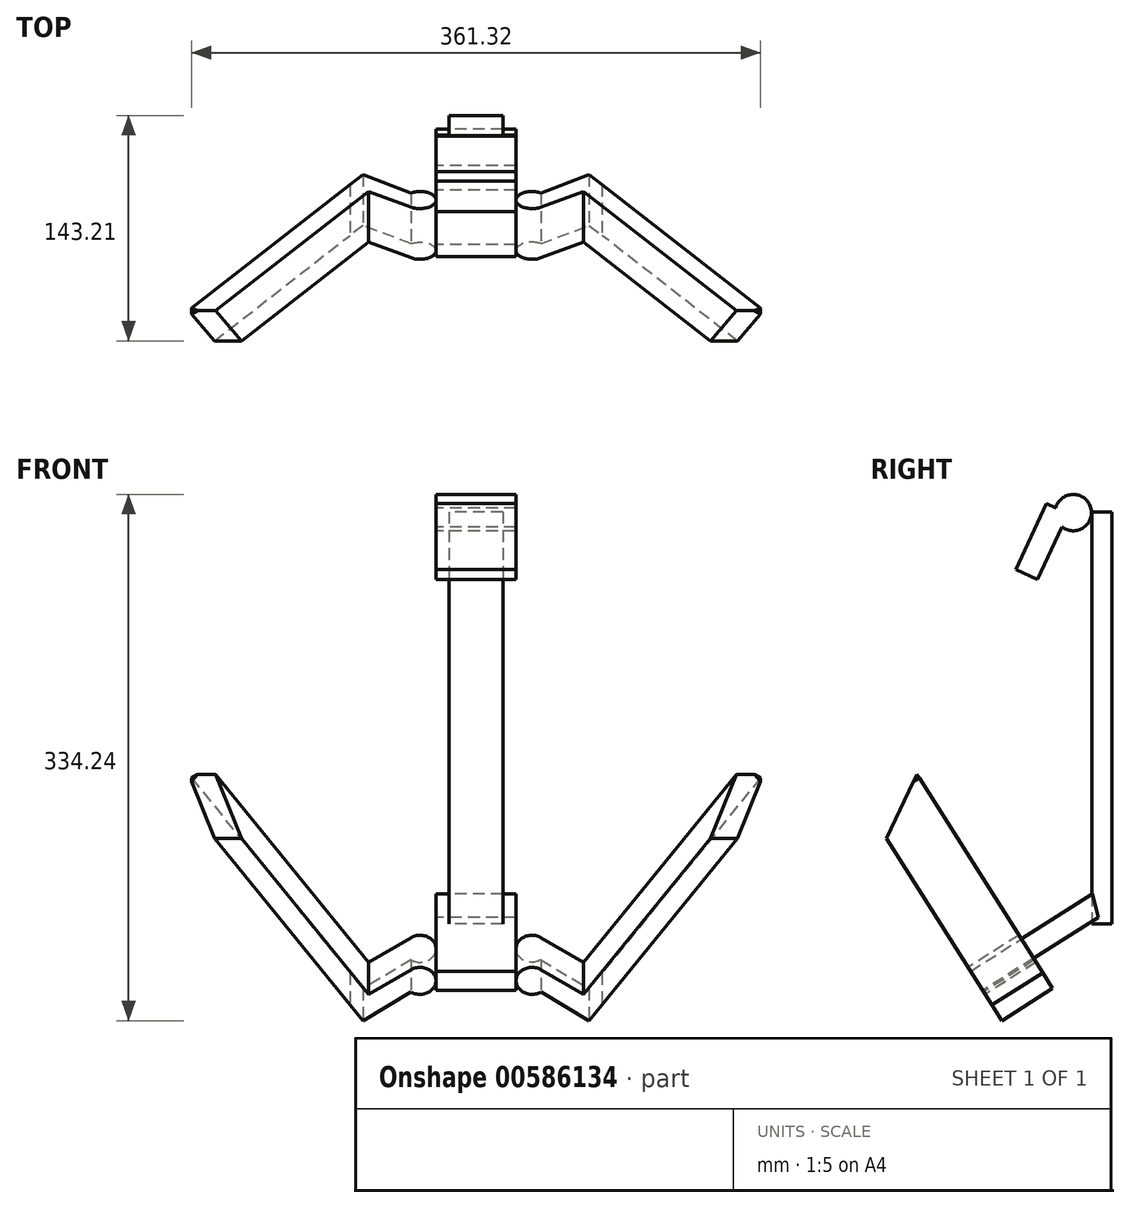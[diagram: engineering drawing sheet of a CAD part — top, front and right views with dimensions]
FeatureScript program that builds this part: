
annotation { "Feature Type Name" : "Feature", "Feature Type Description" : "" }
export const myFeature = defineFeature(function(context is Context, id is Id, definition is map)
    precondition{}
    {
        {
            var Q0;
            Q0=qCreatedBy(makeId("Front.planeOp"),FACE);
            var sketch = newSketch(context, id + "F0", { "sketchPlane" : qUnion([Q0])});
            skLineSegment(sketch, "E0.bottom", {"start": v(17.06, 130.82) * mm, "end": v(-17.06, 130.82) * mm});
            skLineSegment(sketch, "E0.top", {"start": v(17.06, -130.82) * mm, "end": v(-17.06, -130.82) * mm});
            skLineSegment(sketch, "E0.left", {"start": v(17.06, 130.82) * mm, "end": v(17.06, -130.82) * mm});
            skLineSegment(sketch, "E0.right", {"start": v(-17.06, 130.82) * mm, "end": v(-17.06, -130.82) * mm});
            skPoint(sketch, "E0.middle", {"position": v(0, 0) * mm});
            skSolve(sketch);
        }
        {
            var Q0;
            Q0 = qSketchRegion(id + "F0", true);
            extrude(context, id + "F1", {"entities" : qUnion([Q0]), "depth" : 12.7 * mm, "offsetDistance" : 25.4 * mm});
        }
        {
            var Q0;
            Q0=qCreatedBy(makeId("Right.planeOp"),FACE);
            var sketch = newSketch(context, id + "F2", { "sketchPlane" : qUnion([Q0])});
            skCircle(sketch, "E1", {"center": v(-24.55, 130.32) * mm, "radius": 11.55 * mm});
            skLineSegment(sketch, "E2", {"start": v(-31.77, 121.3) * mm, "end": v(-47.3, 87.72) * mm});
            skLineSegment(sketch, "E3", {"start": v(-47.3, 87.72) * mm, "end": v(-61.05, 94.08) * mm});
            skLineSegment(sketch, "E4", {"start": v(-61.05, 94.08) * mm, "end": v(-41.65, 136.02) * mm});
            skLineSegment(sketch, "E5", {"start": v(-41.65, 136.02) * mm, "end": v(-35.72, 133.28) * mm});
            skSolve(sketch);
        }
        {
            var Q0;
            Q0 = qSketchRegion(id + "F2", true);
            extrude(context, id + "F3", {"entities" : qUnion([Q0]), "depth" : 25.4 * mm, "offsetDistance" : 25.4 * mm, "hasSecondDirection" : true, "secondDirectionOppositeDirection" : true, "secondDirectionDepth" : 25.4 * mm});
        }
        {
            var Q0;
            Q0=makeQuery(id+"F3.opExtrude","SWEPT_BODY",BODY,{"disambiguationData":[OSD([sQuery(id+"F2.wireOp",EDGE,"E1"),sQuery(id+"F2.wireOp",EDGE,"E2"),sQuery(id+"F2.wireOp",EDGE,"E3"),sQuery(id+"F2.wireOp",EDGE,"E4"),sQuery(id+"F2.wireOp",EDGE,"E5")])]});
            var Q1;
            Q1=qCreatedBy(makeId("Top.planeOp"),FACE);
            mirror(context, id + "F4", {"entities" : qUnion([Q0]), "mirrorPlane" : qUnion([Q1])});
        }
        {
            var Q0;
            Q0=makeQuery(id+"F4.opPattern","COPY",BODY,{"derivedFrom":makeQuery(id+"F3.opExtrude","SWEPT_BODY",BODY,{"disambiguationData":[OSD([sQuery(id+"F2.wireOp",EDGE,"E1"),sQuery(id+"F2.wireOp",EDGE,"E2"),sQuery(id+"F2.wireOp",EDGE,"E3"),sQuery(id+"F2.wireOp",EDGE,"E4"),sQuery(id+"F2.wireOp",EDGE,"E5")])]}),"instanceName":"1"});
            deleteBodies(context, id + "F5", {"entities" : qUnion([Q0])});
        }
        {
            var Q0;
            Q0=qCreatedBy(makeId("Right.planeOp"),FACE);
            var sketch = newSketch(context, id + "F6", { "sketchPlane" : qUnion([Q0])});
            skLineSegment(sketch, "E6", {"start": v(-37.8, -145.19) * mm, "end": v(-82.02, -173.2) * mm});
            skLineSegment(sketch, "E7", {"start": v(-82.02, -173.2) * mm, "end": v(-89.77, -160.96) * mm});
            skLineSegment(sketch, "E8", {"start": v(-89.77, -160.96) * mm, "end": v(-46.36, -133.47) * mm});
            skLineSegment(sketch, "E9", {"start": v(-46.36, -133.47) * mm, "end": v(-12.31, -111.9) * mm});
            skLineSegment(sketch, "E10", {"start": v(-37.8, -145.19) * mm, "end": v(-8.51, -126.64) * mm});
            skLineSegment(sketch, "E11", {"start": v(-8.51, -126.64) * mm, "end": v(-12.31, -111.9) * mm});
            skSolve(sketch);
        }
        {
            var Q0;
            Q0 = qSketchRegion(id + "F6", true);
            extrude(context, id + "F7", {"entities" : qUnion([Q0]), "depth" : 25.4 * mm, "offsetDistance" : 25.4 * mm, "hasSecondDirection" : true, "secondDirectionOppositeDirection" : true, "secondDirectionDepth" : 25.4 * mm});
        }
        {
            var Q0;
            Q0=makeQuery(id+"F7.opExtrude","SWEPT_FACE",FACE,{"disambiguationData":[OSD([sQuery(id+"F6.wireOp",EDGE,"E7")])]});
            var sketch = newSketch(context, id + "F8", { "sketchPlane" : qUnion([Q0])});
            skCircle(sketch, "E12", {"center": v(-35.54, -95.2) * mm, "radius": 10.14 * mm});
            skPoint(sketch, "E12.centerSnap0", {"position": v(-25.4, -95.2) * mm});
            skLineSegment(sketch, "E13", {"start": v(-41.21, -103.6) * mm, "end": v(-71.78, -125.13) * mm});
            skLineSegment(sketch, "E14", {"start": v(-71.78, -125.13) * mm, "end": v(-80.02, -113.44) * mm});
            skLineSegment(sketch, "E15", {"start": v(-80.02, -113.44) * mm, "end": v(-41.28, -86.84) * mm});
            skSolve(sketch);
        }
        {
            var Q0;
            Q0 = qSketchRegion(id + "F8", true);
            extrude(context, id + "F9", {"entities" : qUnion([Q0]), "operationType" : NewBodyOperationType.ADD, "oppositeDirection" : true, "depth" : 38.1 * mm, "offsetDistance" : 25.4 * mm});
        }
        {
            var Q0;
            Q0=makeQuery(id+"F9.opExtrude","SWEPT_BODY",BODY,{"disambiguationData":[OSD([sQuery(id+"F8.wireOp",EDGE,"E12"),sQuery(id+"F8.wireOp",EDGE,"E13"),sQuery(id+"F8.wireOp",EDGE,"E14"),sQuery(id+"F8.wireOp",EDGE,"E15")])]});
            var Q1;
            Q1=qCreatedBy(makeId("Right.planeOp"),FACE);
            mirror(context, id + "F10", {"operationType" : NewBodyOperationType.ADD, "entities" : qUnion([Q0]), "mirrorPlane" : qUnion([Q1])});
        }
        {
            var Q0;
            Q0=makeQuery(id+"F9.opExtrude","SWEPT_FACE",FACE,{"disambiguationData":[OSD([sQuery(id+"F8.wireOp",EDGE,"E15")])]});
            var sketch = newSketch(context, id + "F11", { "sketchPlane" : qUnion([Q0])});
            skLineSegment(sketch, "E16.bottom", {"start": v(-130.17, -123.86) * mm, "end": v(-116.05, -123.86) * mm});
            skLineSegment(sketch, "E16.top", {"start": v(-130.17, -161.96) * mm, "end": v(-116.05, -161.96) * mm});
            skLineSegment(sketch, "E16.left", {"start": v(-130.17, -123.86) * mm, "end": v(-130.17, -161.96) * mm});
            skLineSegment(sketch, "E16.right", {"start": v(-116.05, -123.86) * mm, "end": v(-116.05, -161.96) * mm});
            skSolve(sketch);
        }
        {
            var Q0;
            Q0=makeQuery(id+"F11.imprint","IMPRINT",FACE,{"disambiguationData":[TD([[makeQuery(id+"F11.imprint","IMPRINT",EDGE,{"derivedFrom":sQuery(id+"F11.wireOp",EDGE,"E16.bottom")}),-1.0]])]});
            extrude(context, id + "F12", {"entities" : qUnion([Q0]), "operationType" : NewBodyOperationType.ADD, "depth" : 177.8 * mm, "offsetDistance" : 25.4 * mm});
        }
        {
            var Q0;
            Q0=makeQuery(id+"F9.opExtrude","SWEPT_BODY",BODY,{"disambiguationData":[OSD([sQuery(id+"F8.wireOp",EDGE,"E12"),sQuery(id+"F8.wireOp",EDGE,"E13"),sQuery(id+"F8.wireOp",EDGE,"E14"),sQuery(id+"F8.wireOp",EDGE,"E15")])]});
            var Q1;
            Q1=qCreatedBy(makeId("Right.planeOp"),FACE);
            mirror(context, id + "F13", {"entities" : qUnion([Q0]), "mirrorPlane" : qUnion([Q1])});
        }
        {
            var Q0;
            Q0=qCreatedBy(makeId("Right.planeOp"),FACE);
            var sketch = newSketch(context, id + "F14", { "sketchPlane" : qUnion([Q0])});
            skLineSegment(sketch, "E17", {"start": v(-41.32, 136.62) * mm, "end": v(-170.9, -134.55) * mm});
            skLineSegment(sketch, "E18", {"start": v(-170.9, -134.55) * mm, "end": v(-170.9, 47.15) * mm});
            skLineSegment(sketch, "E19", {"start": v(-170.9, 47.15) * mm, "end": v(-87.38, 40.23) * mm});
            skSolve(sketch);
        }
        {
            var Q0;
            Q0 = qSketchRegion(id + "F14", true);
            extrude(context, id + "F15", {"entities" : qUnion([Q0]), "operationType" : NewBodyOperationType.REMOVE, "oppositeDirection" : true, "depth" : 508 * mm, "offsetDistance" : 25.4 * mm, "hasSecondDirection" : true, "secondDirectionOppositeDirection" : false, "secondDirectionDepth" : 508 * mm});
        }
        {
            var Q0;
            Q0=makeQuery(id+"F13.opPattern","COPY",BODY,{"derivedFrom":makeQuery(id+"F9.opExtrude","SWEPT_BODY",BODY,{"disambiguationData":[OSD([sQuery(id+"F8.wireOp",EDGE,"E12"),sQuery(id+"F8.wireOp",EDGE,"E13"),sQuery(id+"F8.wireOp",EDGE,"E14"),sQuery(id+"F8.wireOp",EDGE,"E15")])]}),"instanceName":"1"});
            deleteBodies(context, id + "F16", {"entities" : qUnion([Q0])});
        }
        {
            var Q0;
            Q0=makeQuery(id+"F10.opPattern","COPY",BODY,{"derivedFrom":makeQuery(id+"F9.opExtrude","SWEPT_BODY",BODY,{"disambiguationData":[OSD([sQuery(id+"F8.wireOp",EDGE,"E12"),sQuery(id+"F8.wireOp",EDGE,"E13"),sQuery(id+"F8.wireOp",EDGE,"E14"),sQuery(id+"F8.wireOp",EDGE,"E15")])]}),"instanceName":"1"});
            deleteBodies(context, id + "F17", {"entities" : qUnion([Q0])});
        }
        {
            var Q0;
            Q0=makeQuery(id+"F9.opExtrude","SWEPT_BODY",BODY,{"disambiguationData":[OSD([sQuery(id+"F8.wireOp",EDGE,"E12"),sQuery(id+"F8.wireOp",EDGE,"E13"),sQuery(id+"F8.wireOp",EDGE,"E14"),sQuery(id+"F8.wireOp",EDGE,"E15")])]});
            var Q1;
            Q1=qCreatedBy(makeId("Right.planeOp"),FACE);
            mirror(context, id + "F18", {"operationType" : NewBodyOperationType.ADD, "entities" : qUnion([Q0]), "mirrorPlane" : qUnion([Q1])});
        }
        {
            var Q0;
            Q0=qCreatedBy(makeId("Right.planeOp"),FACE);
            var sketch = newSketch(context, id + "F19", { "sketchPlane" : qUnion([Q0])});
            skLineSegment(sketch, "E20", {"start": v(-145, -76.44) * mm, "end": v(-43.4, 137.63) * mm});
            skLineSegment(sketch, "E21", {"start": v(-43.4, 137.63) * mm, "end": v(-175.9, -141.57) * mm});
            skLineSegment(sketch, "E22", {"start": v(-175.9, -141.57) * mm, "end": v(-240.48, -110.92) * mm});
            skLineSegment(sketch, "E23", {"start": v(-240.48, -110.92) * mm, "end": v(-107.67, 168.9) * mm});
            skLineSegment(sketch, "E24", {"start": v(-107.67, 168.9) * mm, "end": v(-43.4, 137.63) * mm});
            skSolve(sketch);
        }
        {
            var Q0;
            Q0 = qSketchRegion(id + "F19", true);
            extrude(context, id + "F20", {"entities" : qUnion([Q0]), "depth" : 228.6 * mm, "offsetDistance" : 25.4 * mm, "hasSecondDirection" : true, "secondDirectionOppositeDirection" : true, "secondDirectionDepth" : 228.6 * mm});
        }
        {
            var Q0;
            Q0=makeQuery(id+"F20.opExtrude","SWEPT_BODY",BODY,{"disambiguationData":[OSD([sQuery(id+"F19.wireOp",EDGE,"E21"),sQuery(id+"F19.wireOp",EDGE,"E22"),sQuery(id+"F19.wireOp",EDGE,"E23"),sQuery(id+"F19.wireOp",EDGE,"E24")])]});
            deleteBodies(context, id + "F21", {"entities" : qUnion([Q0])});
        }
    });
